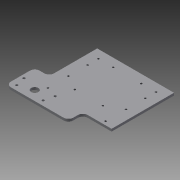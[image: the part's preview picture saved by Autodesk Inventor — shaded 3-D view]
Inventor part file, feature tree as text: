
AUTODESK INVENTOR PART (.ipt)
format: ipt  version: 2013 (Build 170138000, 138)  size: 203,776 bytes
history: native  units: in
note: dims shown in document units (in); Inventor stores cm internally (conversion verified against a paired STEP export)
features: hole x3, sketch x3, other x2, sheet_metal_op x1
ambient origin geometry x8: Origin, YZ Plane, XZ Plane, XY Plane, X Axis, Y Axis, Z Axis, Center Point
feature tree (9):
  sheet_metal_op  "Face2"
  hole  "Hole2"  [1 undecoded]
  hole  "Hole3"  [1 undecoded]
  hole  "Hole5"  [1 undecoded]
  other  "Plate2"
  sketch  "Sketch5"  dims[d15=0.25in d16=0.25in]
  sketch  "Sketch12"  dims[d27=1.0in d28=1.0in]
  sketch  "Sketch14"  dims[d30=5.25in d31=0.196in d32=0.75in d33=0.375in d34=0.25in d35=0.5635in d36=1.0in d37=0.8108in d62=0.875in d64=1.5in d67=0.5in d69=0.5in d89=2.0in d90=2.0in d91=1.0in d93=6.0in d94=1.0in d97=0.75in d98=0.75in d99=0.375in d100=0.25in d101=0.5635in d102=0.25in d103=0.8108in d105=3.0in d106=0.5in d107=2.0in d108=8.0in d109=5.0in d110=6.5in d111=1.5in d129=2.0in d130=0.25in d135=0.25in d136=1.0in d137=0.5in d138=3.25in d139=1.625in d140=0.25in d141=0.75in d142=0.375in d143=0.25in d144=0.5635in d145=0.25in d146=0.8108in d147=2.54in d148=2.54in d149=4.0in]
  other  "Definition1"
note: 3 required parameter values undecoded (feature->parameter linkage not recoverable at this tier; creation-order binding heuristic only, values carry confidence <= 0.55)
